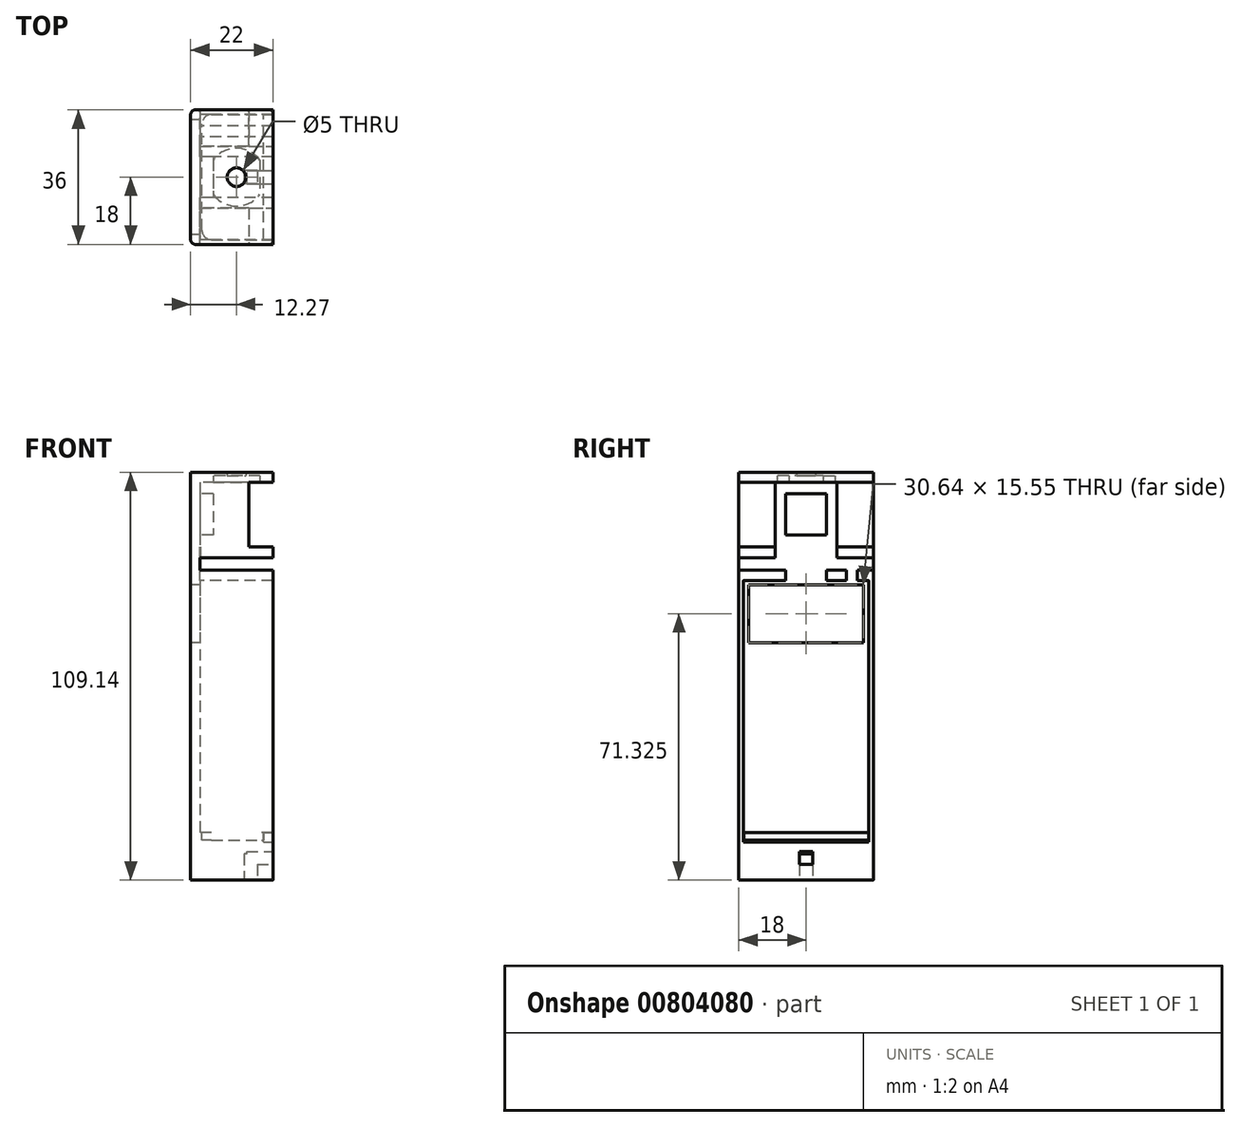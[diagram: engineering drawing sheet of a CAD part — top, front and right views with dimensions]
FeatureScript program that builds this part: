
annotation { "Feature Type Name" : "Feature", "Feature Type Description" : "" }
export const myFeature = defineFeature(function(context is Context, id is Id, definition is map)
    precondition{}
    {
        {
            var Q0;
            Q0=qCreatedBy(makeId("Right.planeOp"),FACE);
            var sketch = newSketch(context, id + "F0", { "sketchPlane" : qUnion([Q0])});
            skLineSegment(sketch, "E0", {"start": v(0, 0) * mm, "end": v(0, 70.44) * mm});
            skLineSegment(sketch, "E1", {"start": v(0, 70.44) * mm, "end": v(0, -68.16) * mm});
            skSolve(sketch);
        }
        {
            var Q0;
            Q0=qCreatedBy(makeId("Right.planeOp"),FACE);
            var sketch = newSketch(context, id + "F1", { "sketchPlane" : qUnion([Q0])});
            skLineSegment(sketch, "E2", {"start": v(0, 0) * mm, "end": v(-18, 0) * mm});
            skLineSegment(sketch, "E3", {"start": v(-18, 0) * mm, "end": v(-18, 100) * mm});
            skLineSegment(sketch, "E4", {"start": v(-18, 100) * mm, "end": v(0, 100) * mm});
            skLineSegment(sketch, "E5.MirrorCS", {"start": v(18, 100) * mm, "end": v(0, 100) * mm});
            skLineSegment(sketch, "E6.MirrorCS", {"start": v(0, 0) * mm, "end": v(18, 0) * mm});
            skLineSegment(sketch, "E7.MirrorCS", {"start": v(18, 0) * mm, "end": v(18, 100) * mm});
            skSolve(sketch);
        }
        {
            var Q0;
            Q0=makeQuery(id+"F1.imprint","IMPRINT",FACE,{"disambiguationData":[TD([[makeQuery(id+"F1.imprint","IMPRINT",EDGE,{"derivedFrom":sQuery(id+"F1.wireOp",EDGE,"E2")}),-1.0]])]});
            extrude(context, id + "F2", {"entities" : qUnion([Q0]), "oppositeDirection" : true, "depth" : 22 * mm, "offsetDistance" : 25.4 * mm});
        }
        {
            var Q0;
            Q0=makeQuery(id+"F2.opExtrude","CAP_FACE",FACE,{"disambiguationData":[OSD([sQuery(id+"F1.wireOp",EDGE,"E2"),sQuery(id+"F1.wireOp",EDGE,"E3"),sQuery(id+"F1.wireOp",EDGE,"E4"),sQuery(id+"F1.wireOp",EDGE,"E5.MirrorCS"),sQuery(id+"F1.wireOp",EDGE,"E6.MirrorCS"),sQuery(id+"F1.wireOp",EDGE,"E7.MirrorCS")])],"isStart":true});
            var Q1;
            Q1=makeQuery(id+"F2.opExtrude","SWEPT_FACE",FACE,{"disambiguationData":[OSD([sQuery(id+"F1.wireOp",EDGE,"E7.MirrorCS")])]});
            var Q2;
            Q2=makeQuery(id+"F2.opExtrude","SWEPT_FACE",FACE,{"disambiguationData":[OSD([sQuery(id+"F1.wireOp",EDGE,"E3")])]});
            shell(context, id + "F3", {"entities" : qUnion([Q0, Q1, Q2]), "thickness" : 2.54 * mm});
        }
        {
            var Q0;
            Q0=makeQuery(id+"F3.opShell","OFFSET_FACE",FACE,{"disambiguationData":[OSD([sQuery(id+"F1.wireOp",EDGE,"E2"),sQuery(id+"F1.wireOp",EDGE,"E6.MirrorCS")])]});
            var sketch = newSketch(context, id + "F4", { "sketchPlane" : qUnion([Q0])});
            skLineSegment(sketch, "E8.bottom", {"start": v(-18.98, -16.75) * mm, "end": v(-0.48, -16.75) * mm});
            skLineSegment(sketch, "E8.top", {"start": v(-18.98, 16.75) * mm, "end": v(-0.48, 16.75) * mm});
            skLineSegment(sketch, "E8.left", {"start": v(-18.98, -16.75) * mm, "end": v(-18.98, 16.75) * mm});
            skLineSegment(sketch, "E8.right", {"start": v(-0.48, -16.75) * mm, "end": v(-0.48, 16.75) * mm});
            skLineSegment(sketch, "E9", {"start": v(0, 0) * mm, "end": v(-19.46, 0) * mm});
            skLineSegment(sketch, "E10", {"start": v(-9.73, -18) * mm, "end": v(-9.73, 18) * mm});
            skSolve(sketch);
        }
        {
            var Q0;
            Q0 = qSketchRegion(id + "F4", true);
            extrude(context, id + "F5", {"entities" : qUnion([Q0]), "operationType" : NewBodyOperationType.REMOVE, "oppositeDirection" : true, "depth" : 2 * mm, "offsetDistance" : 25.4 * mm});
        }
        {
            var Q0;
            Q0=makeQuery(id+"F5.boolean.opBoolean","COPY",EDGE,{"derivedFrom":makeQuery(id+"F5.opExtrude","SWEPT_EDGE",EDGE,{"disambiguationData":[OSD([sQuery(id+"F4.wireOp",EDGE,"E8.bottom"),sQuery(id+"F4.wireOp",EDGE,"E8.left")])]})});
            var Q1;
            Q1=makeQuery(id+"F5.boolean.opBoolean","COPY",EDGE,{"derivedFrom":makeQuery(id+"F5.opExtrude","SWEPT_EDGE",EDGE,{"disambiguationData":[OSD([sQuery(id+"F4.wireOp",EDGE,"E8.top"),sQuery(id+"F4.wireOp",EDGE,"E8.left")])]})});
            var Q2;
            Q2=makeQuery(id+"F5.boolean.opBoolean","COPY",EDGE,{"derivedFrom":makeQuery(id+"F5.opExtrude","SWEPT_EDGE",EDGE,{"disambiguationData":[OSD([sQuery(id+"F4.wireOp",EDGE,"E8.top"),sQuery(id+"F4.wireOp",EDGE,"E8.right")])]})});
            var Q3;
            Q3=makeQuery(id+"F5.boolean.opBoolean","COPY",EDGE,{"derivedFrom":makeQuery(id+"F5.opExtrude","SWEPT_EDGE",EDGE,{"disambiguationData":[OSD([sQuery(id+"F4.wireOp",EDGE,"E8.bottom"),sQuery(id+"F4.wireOp",EDGE,"E8.right")])]})});
            fillet(context, id + "F6", {"entities" : qUnion([Q0, Q1, Q2, Q3]), "radius" : 2.54 * mm, "tangentPropagation" : true, "allowEdgeOverflow" : false});
        }
        {
            var Q0;
            {var subQ0=sQuery(id+"F1.wireOp",EDGE,"E7.MirrorCS");var subQ1=sQuery(id+"F1.wireOp",EDGE,"E6.MirrorCS");var subQ2=sQuery(id+"F1.wireOp",EDGE,"E5.MirrorCS");var subQ3=sQuery(id+"F1.wireOp",EDGE,"E4");var subQ4=sQuery(id+"F1.wireOp",EDGE,"E3");var subQ5=sQuery(id+"F1.wireOp",EDGE,"E2");Q0=makeQuery(id+"F3.opShell","OFFSET_FACE",FACE,{"disambiguationData":[OSD([subQ5,subQ4,subQ3,subQ2,subQ1,subQ0]),TDD([makeQuery(id+"F2.opExtrude","CAP_FACE",FACE,{"disambiguationData":[OSD([subQ5,subQ4,subQ3,subQ2,subQ1,subQ0])],"isStart":false})])]});}
            var sketch = newSketch(context, id + "F7", { "sketchPlane" : qUnion([Q0])});
            skLineSegment(sketch, "E11.bottom", {"start": v(-18, 70.04) * mm, "end": v(-5.5, 70.04) * mm});
            skLineSegment(sketch, "E11.top", {"start": v(-18, 72.77) * mm, "end": v(-5.5, 72.77) * mm});
            skLineSegment(sketch, "E11.left", {"start": v(-18, 70.04) * mm, "end": v(-18, 72.77) * mm});
            skLineSegment(sketch, "E11.right", {"start": v(-5.5, 70.04) * mm, "end": v(-5.5, 72.77) * mm});
            skLineSegment(sketch, "E12.bottom", {"start": v(5.5, 72.77) * mm, "end": v(10.75, 72.77) * mm});
            skLineSegment(sketch, "E12.top", {"start": v(5.5, 70.04) * mm, "end": v(10.75, 70.04) * mm});
            skLineSegment(sketch, "E12.left", {"start": v(5.5, 72.77) * mm, "end": v(5.5, 70.04) * mm});
            skLineSegment(sketch, "E12.right", {"start": v(10.75, 72.77) * mm, "end": v(10.75, 70.04) * mm});
            skLineSegment(sketch, "E13", {"start": v(-16.75, 70.04) * mm, "end": v(-16.75, 72.77) * mm});
            skPoint(sketch, "E14.end.orphan", {"position": v(-14.33, 70.04) * mm});
            skLineSegment(sketch, "E15.bottom", {"start": v(18, 70.04) * mm, "end": v(13.7, 70.04) * mm});
            skLineSegment(sketch, "E15.top", {"start": v(18, 72.77) * mm, "end": v(13.7, 72.77) * mm});
            skLineSegment(sketch, "E15.left", {"start": v(18, 70.04) * mm, "end": v(18, 72.77) * mm});
            skLineSegment(sketch, "E15.right", {"start": v(13.7, 70.04) * mm, "end": v(13.7, 72.77) * mm});
            skLineSegment(sketch, "E16.bottom", {"start": v(-18, 76.1) * mm, "end": v(-5.5, 76.1) * mm});
            skLineSegment(sketch, "E16.top", {"start": v(-18, 79.1) * mm, "end": v(-5.5, 79.1) * mm});
            skLineSegment(sketch, "E16.left", {"start": v(-18, 76.1) * mm, "end": v(-18, 79.1) * mm});
            skLineSegment(sketch, "E16.right", {"start": v(-5.5, 76.1) * mm, "end": v(-5.5, 79.1) * mm});
            skLineSegment(sketch, "E17.bottom", {"start": v(5.5, 76.1) * mm, "end": v(18, 76.1) * mm});
            skLineSegment(sketch, "E17.top", {"start": v(5.5, 79.1) * mm, "end": v(18, 79.1) * mm});
            skLineSegment(sketch, "E17.left", {"start": v(5.5, 76.1) * mm, "end": v(5.5, 79.1) * mm});
            skLineSegment(sketch, "E17.right", {"start": v(18, 76.1) * mm, "end": v(18, 79.1) * mm});
            skSolve(sketch);
        }
        {
            var Q0;
            Q0=makeQuery(id+"F3.opShell","OFFSET_FACE",FACE,{"disambiguationData":[OSD([sQuery(id+"F1.wireOp",EDGE,"E4"),sQuery(id+"F1.wireOp",EDGE,"E5.MirrorCS")])]});
            var sketch = newSketch(context, id + "F8", { "sketchPlane" : qUnion([Q0])});
            skArc(sketch, "E18", {"start": v(-3.48, 4.58) * mm, "mid": v(-9.73, 7.75) * mm, "end": v(-15.98, 4.58) * mm});
            skPoint(sketch, "E18.centerSnap0", {"position": v(-19.46, 0) * mm});
            skPoint(sketch, "E18.centerSnap1", {"position": v(-9.73, -18) * mm});
            skLineSegment(sketch, "E19.bottom", {"start": v(-3.48, -4.58) * mm, "end": v(-15.98, -4.58) * mm});
            skLineSegment(sketch, "E19.top", {"start": v(-3.48, 4.58) * mm, "end": v(-15.98, 4.58) * mm});
            skLineSegment(sketch, "E19.left", {"start": v(-3.48, -4.58) * mm, "end": v(-3.48, 4.58) * mm});
            skLineSegment(sketch, "E19.right", {"start": v(-15.98, -4.58) * mm, "end": v(-15.98, 4.58) * mm});
            skArc(sketch, "E20.trimOffspring", {"start": v(-15.98, -4.58) * mm, "mid": v(-9.73, -7.75) * mm, "end": v(-3.48, -4.58) * mm});
            skSolve(sketch);
        }
        {
            var Q0;
            Q0 = qSketchRegion(id + "F8", true);
            extrude(context, id + "F9", {"entities" : qUnion([Q0]), "operationType" : NewBodyOperationType.REMOVE, "oppositeDirection" : true, "depth" : 0.64 * mm, "offsetDistance" : 25.4 * mm});
        }
        {
            var Q0;
            Q0 = qSketchRegion(id + "F7", true);
            extrude(context, id + "F10", {"entities" : qUnion([Q0]), "operationType" : NewBodyOperationType.ADD, "depth" : 19.46 * mm, "offsetDistance" : 25.4 * mm});
        }
        {
            var Q0;
            Q0=makeQuery(id+"F9.boolean.opBoolean","COPY",FACE,{"derivedFrom":makeQuery(id+"F9.opExtrude","CAP_FACE",FACE,{"disambiguationData":[OSD([sQuery(id+"F8.wireOp",EDGE,"E18"),sQuery(id+"F8.wireOp",EDGE,"E19.left"),sQuery(id+"F8.wireOp",EDGE,"E19.right"),sQuery(id+"F8.wireOp",EDGE,"E20.trimOffspring")])],"isStart":false})});
            var sketch = newSketch(context, id + "F11", { "sketchPlane" : qUnion([Q0])});
            skCircle(sketch, "E21", {"center": v(-9.73, 0) * mm, "radius": 2.5 * mm});
            skSolve(sketch);
        }
        {
            var Q0;
            Q0=makeQuery(id+"F11.imprint","IMPRINT",FACE,{"disambiguationData":[TD([[makeQuery(id+"F11.imprint","IMPRINT",EDGE,{"derivedFrom":sQuery(id+"F11.wireOp",EDGE,"E21")}),1.0]])]});
            extrude(context, id + "F12", {"entities" : qUnion([Q0]), "operationType" : NewBodyOperationType.REMOVE, "oppositeDirection" : true, "depth" : 2.26 * mm, "offsetDistance" : 25.4 * mm});
        }
        {
            var Q0;
            Q0=makeQuery(id+"F3.opShell","OFFSET_FACE",FACE,{"disambiguationData":[OSD([sQuery(id+"F1.wireOp",EDGE,"E4"),sQuery(id+"F1.wireOp",EDGE,"E5.MirrorCS")])]});
            extrude(context, id + "F13", {"entities" : qUnion([Q0]), "operationType" : NewBodyOperationType.ADD, "depth" : 1.14 * mm, "offsetDistance" : 25.4 * mm});
        }
        {
            var Q0;
            Q0=makeQuery(id+"F2.opExtrude","SWEPT_FACE",FACE,{"disambiguationData":[OSD([sQuery(id+"F1.wireOp",EDGE,"E4"),sQuery(id+"F1.wireOp",EDGE,"E5.MirrorCS")])]});
            extrude(context, id + "F14", {"entities" : qUnion([Q0]), "operationType" : NewBodyOperationType.REMOVE, "oppositeDirection" : true, "depth" : 1.02 * mm, "offsetDistance" : 25.4 * mm});
        }
        {
            var Q0;
            {var subQ0=sQuery(id+"F1.wireOp",EDGE,"E7.MirrorCS");var subQ1=sQuery(id+"F1.wireOp",EDGE,"E6.MirrorCS");var subQ2=sQuery(id+"F1.wireOp",EDGE,"E5.MirrorCS");var subQ3=sQuery(id+"F1.wireOp",EDGE,"E4");var subQ4=sQuery(id+"F1.wireOp",EDGE,"E3");var subQ5=sQuery(id+"F1.wireOp",EDGE,"E2");Q0=makeQuery(id+"F3.opShell","OFFSET_FACE",FACE,{"disambiguationData":[OSD([subQ5,subQ4,subQ3,subQ2,subQ1,subQ0]),TDD([makeQuery(id+"F2.opExtrude","CAP_FACE",FACE,{"disambiguationData":[OSD([subQ5,subQ4,subQ3,subQ2,subQ1,subQ0])],"isStart":false})])]});}
            var sketch = newSketch(context, id + "F15", { "sketchPlane" : qUnion([Q0])});
            skLineSegment(sketch, "E22", {"start": v(0, 87.22) * mm, "end": v(-8.25, 87.22) * mm});
            skLineSegment(sketch, "E23", {"start": v(-8.25, 87.22) * mm, "end": v(8.25, 87.22) * mm});
            skLineSegment(sketch, "E24.bottom", {"start": v(18, 96.32) * mm, "end": v(8.25, 96.32) * mm});
            skLineSegment(sketch, "E24.top", {"start": v(18, 79.1) * mm, "end": v(8.25, 79.1) * mm});
            skLineSegment(sketch, "E24.left", {"start": v(18, 96.32) * mm, "end": v(18, 79.1) * mm});
            skLineSegment(sketch, "E24.right", {"start": v(8.25, 96.32) * mm, "end": v(8.25, 79.1) * mm});
            skLineSegment(sketch, "E25.bottom", {"start": v(-8.25, 79.1) * mm, "end": v(-18, 79.1) * mm});
            skLineSegment(sketch, "E25.top", {"start": v(-8.25, 96.32) * mm, "end": v(-18, 96.32) * mm});
            skLineSegment(sketch, "E25.left", {"start": v(-8.25, 79.1) * mm, "end": v(-8.25, 96.32) * mm});
            skLineSegment(sketch, "E25.right", {"start": v(-18, 79.1) * mm, "end": v(-18, 96.32) * mm});
            skSolve(sketch);
        }
        {
            var Q0;
            Q0 = qSketchRegion(id + "F15", true);
            extrude(context, id + "F16", {"entities" : qUnion([Q0]), "operationType" : NewBodyOperationType.ADD, "depth" : 13 * mm, "offsetDistance" : 25.4 * mm});
        }
        {
            var Q0;
            {var subQ0=sQuery(id+"F1.wireOp",EDGE,"E7.MirrorCS");var subQ1=sQuery(id+"F1.wireOp",EDGE,"E6.MirrorCS");var subQ2=sQuery(id+"F1.wireOp",EDGE,"E5.MirrorCS");var subQ3=sQuery(id+"F1.wireOp",EDGE,"E4");var subQ4=sQuery(id+"F1.wireOp",EDGE,"E3");var subQ5=sQuery(id+"F1.wireOp",EDGE,"E2");Q0=makeQuery(id+"F3.opShell","OFFSET_FACE",FACE,{"disambiguationData":[OSD([subQ5,subQ4,subQ3,subQ2,subQ1,subQ0]),TDD([makeQuery(id+"F2.opExtrude","CAP_FACE",FACE,{"disambiguationData":[OSD([subQ5,subQ4,subQ3,subQ2,subQ1,subQ0])],"isStart":false})])]});}
            var sketch = newSketch(context, id + "F17", { "sketchPlane" : qUnion([Q0])});
            skLineSegment(sketch, "E26.bottom", {"start": v(-18, 2.54) * mm, "end": v(-16.75, 2.54) * mm});
            skLineSegment(sketch, "E26.top", {"start": v(-18, 70.04) * mm, "end": v(-16.75, 70.04) * mm});
            skLineSegment(sketch, "E26.left", {"start": v(-18, 2.54) * mm, "end": v(-18, 70.04) * mm});
            skLineSegment(sketch, "E26.right", {"start": v(-16.75, 2.54) * mm, "end": v(-16.75, 70.04) * mm});
            skLineSegment(sketch, "E27.bottom", {"start": v(18, 70.04) * mm, "end": v(16.75, 70.04) * mm});
            skLineSegment(sketch, "E27.top", {"start": v(18, 2.54) * mm, "end": v(16.75, 2.54) * mm});
            skLineSegment(sketch, "E27.left", {"start": v(18, 70.04) * mm, "end": v(18, 2.54) * mm});
            skLineSegment(sketch, "E27.right", {"start": v(16.75, 70.04) * mm, "end": v(16.75, 2.54) * mm});
            skSolve(sketch);
        }
        {
            var Q0;
            Q0 = qSketchRegion(id + "F17", true);
            extrude(context, id + "F18", {"entities" : qUnion([Q0]), "operationType" : NewBodyOperationType.ADD, "depth" : 19.46 * mm, "offsetDistance" : 25.4 * mm});
        }
        {
            var Q0;
            Q0=makeQuery(id+"F2.opExtrude","CAP_EDGE",EDGE,{"disambiguationData":[OSD([sQuery(id+"F1.wireOp",EDGE,"E7.MirrorCS")])],"isStart":false});
            var Q1;
            Q1=makeQuery(id+"F2.opExtrude","CAP_EDGE",EDGE,{"disambiguationData":[OSD([sQuery(id+"F1.wireOp",EDGE,"E3")])],"isStart":false});
            var Q2;
            Q2=makeQuery(id+"F18.boolean.opBoolean","MERGE",EDGE,{"derivedFrom":[makeQuery(id+"F2.opExtrude","CAP_EDGE",EDGE,{"disambiguationData":[OSD([sQuery(id+"F1.wireOp",EDGE,"E3")])],"isStart":true}),makeQuery(id+"F10.opExtrude","CAP_EDGE",EDGE,{"disambiguationData":[OSD([sQuery(id+"F7.wireOp",EDGE,"E11.left")])],"isStart":false}),makeQuery(id+"F18.opExtrude","CAP_EDGE",EDGE,{"disambiguationData":[OSD([sQuery(id+"F17.wireOp",EDGE,"E26.left")])],"isStart":false})]});
            var Q3;
            Q3=makeQuery(id+"F18.boolean.opBoolean","MERGE",EDGE,{"derivedFrom":[makeQuery(id+"F2.opExtrude","CAP_EDGE",EDGE,{"disambiguationData":[OSD([sQuery(id+"F1.wireOp",EDGE,"E7.MirrorCS")])],"isStart":true}),makeQuery(id+"F10.opExtrude","CAP_EDGE",EDGE,{"disambiguationData":[OSD([sQuery(id+"F7.wireOp",EDGE,"E15.left")])],"isStart":false}),makeQuery(id+"F18.opExtrude","CAP_EDGE",EDGE,{"disambiguationData":[OSD([sQuery(id+"F17.wireOp",EDGE,"E27.left")])],"isStart":false})]});
            var Q4;
            Q4=makeQuery(id+"F14.boolean.opBoolean","COPY",EDGE,{"derivedFrom":makeQuery(id+"F14.opExtrude","CAP_EDGE",EDGE,{"disambiguationData":[OSD([sQuery(id+"F1.wireOp",EDGE,"E5.MirrorCS"),sQuery(id+"F1.wireOp",EDGE,"E7.MirrorCS")])],"isStart":false})});
            var Q5;
            Q5=makeQuery(id+"F14.boolean.opBoolean","COPY",EDGE,{"derivedFrom":makeQuery(id+"F14.opExtrude","CAP_EDGE",EDGE,{"disambiguationData":[OSD([sQuery(id+"F1.wireOp",EDGE,"E3"),sQuery(id+"F1.wireOp",EDGE,"E4")])],"isStart":false})});
            var Q6;
            {var subQ0=sQuery(id+"F1.wireOp",EDGE,"E5.MirrorCS");var subQ1=sQuery(id+"F1.wireOp",EDGE,"E4");Q6=makeQuery(id+"F14.boolean.opBoolean","COPY",EDGE,{"derivedFrom":makeQuery(id+"F14.opExtrude","CAP_EDGE",EDGE,{"disambiguationData":[OSD([subQ1,subQ0]),TDD([makeQuery(id+"F2.opExtrude","CAP_EDGE",EDGE,{"disambiguationData":[OSD([subQ1,subQ0])],"isStart":false})])],"isStart":false})});}
            fillet(context, id + "F19", {"entities" : qUnion([Q0, Q1, Q2, Q3, Q4, Q5, Q6]), "radius" : 1.27 * mm, "tangentPropagation" : true, "allowEdgeOverflow" : false});
        }
        {
            var Q0;
            Q0=makeQuery(id+"F2.opExtrude","SWEPT_FACE",FACE,{"disambiguationData":[OSD([sQuery(id+"F1.wireOp",EDGE,"E2"),sQuery(id+"F1.wireOp",EDGE,"E6.MirrorCS")])]});
            var sketch = newSketch(context, id + "F20", { "sketchPlane" : qUnion([Q0])});
            skSolve(sketch);
        }
        {
            var Q0;
            Q0 = qSketchRegion(id + "F20", true);
            var Q1;
            {var subQ1=sQuery(id+"F1.wireOp",EDGE,"E2");var subQ3=sQuery(id+"F1.wireOp",EDGE,"E3");Q1=makeQuery(id+"F20.imprint","IMPRINT",FACE,{"disambiguationData":[TD([[makeQuery(id+"F20.imprint","IMPRINT",EDGE,{"derivedFrom":makeQuery(id+"F2.opExtrude","SWEPT_EDGE",EDGE,{"disambiguationData":[OSD([subQ1,subQ3])]})}),-1.0]])]});}
            extrude(context, id + "F21", {"entities" : qUnion([Q0, Q1]), "operationType" : NewBodyOperationType.ADD, "depth" : 10.16 * mm, "offsetDistance" : 25.4 * mm});
        }
        {
            var Q0;
            {var subQ0=sQuery(id+"F1.wireOp",EDGE,"E6.MirrorCS");var subQ1=sQuery(id+"F1.wireOp",EDGE,"E2");var subQ2=sQuery(id+"F1.wireOp",EDGE,"E7.MirrorCS");var subQ3=sQuery(id+"F1.wireOp",EDGE,"E5.MirrorCS");var subQ4=sQuery(id+"F1.wireOp",EDGE,"E4");var subQ5=sQuery(id+"F1.wireOp",EDGE,"E3");Q0=makeQuery(id+"F21.boolean.opBoolean","MERGE",FACE,{"derivedFrom":[makeQuery(id+"F19.opFillet","SPLIT",FACE,{"disambiguationData":[OD(2.0)],"derivedFrom":makeQuery(id+"F18.boolean.opBoolean","MERGE",FACE,{"derivedFrom":[makeQuery(id+"F3.opShell","OFFSET_FACE",FACE,{"disambiguationData":[OSD([subQ1,subQ5,subQ4,subQ3,subQ0,subQ2]),TDD([makeQuery(id+"F2.opExtrude","CAP_FACE",FACE,{"disambiguationData":[OSD([subQ1,subQ5,subQ4,subQ3,subQ0,subQ2])],"isStart":true})])]}),makeQuery(id+"F10.opExtrude","CAP_FACE",FACE,{"disambiguationData":[OSD([sQuery(id+"F7.wireOp",EDGE,"E11.bottom"),sQuery(id+"F7.wireOp",EDGE,"E11.top"),sQuery(id+"F7.wireOp",EDGE,"E11.left"),sQuery(id+"F7.wireOp",EDGE,"E11.right")])],"isStart":false}),makeQuery(id+"F10.opExtrude","CAP_FACE",FACE,{"disambiguationData":[OSD([sQuery(id+"F7.wireOp",EDGE,"E15.bottom"),sQuery(id+"F7.wireOp",EDGE,"E15.top"),sQuery(id+"F7.wireOp",EDGE,"E15.left"),sQuery(id+"F7.wireOp",EDGE,"E15.right")])],"isStart":false}),makeQuery(id+"F18.opExtrude","CAP_FACE",FACE,{"disambiguationData":[OSD([sQuery(id+"F17.wireOp",EDGE,"E26.bottom"),sQuery(id+"F17.wireOp",EDGE,"E26.top"),sQuery(id+"F17.wireOp",EDGE,"E26.left"),sQuery(id+"F17.wireOp",EDGE,"E26.right")])],"isStart":false}),makeQuery(id+"F18.opExtrude","CAP_FACE",FACE,{"disambiguationData":[OSD([sQuery(id+"F17.wireOp",EDGE,"E27.bottom"),sQuery(id+"F17.wireOp",EDGE,"E27.top"),sQuery(id+"F17.wireOp",EDGE,"E27.left"),sQuery(id+"F17.wireOp",EDGE,"E27.right")])],"isStart":false})]})}),makeQuery(id+"F21.opExtrude","SWEPT_FACE",FACE,{"disambiguationData":[OSD([subQ1,subQ0]),TDD([makeQuery(id+"F20.imprint","IMPRINT",EDGE,{"derivedFrom":makeQuery(id+"F2.opExtrude","CAP_EDGE",EDGE,{"disambiguationData":[OSD([subQ1,subQ0])],"isStart":true})})])]})]});}
            var sketch = newSketch(context, id + "F22", { "sketchPlane" : qUnion([Q0])});
            skLineSegment(sketch, "E28.bottom", {"start": v(1.75, -5.97) * mm, "end": v(-1.75, -5.97) * mm});
            skLineSegment(sketch, "E28.top", {"start": v(1.75, -2.47) * mm, "end": v(-1.75, -2.47) * mm});
            skLineSegment(sketch, "E28.left", {"start": v(1.75, -5.97) * mm, "end": v(1.75, -2.47) * mm});
            skLineSegment(sketch, "E28.right", {"start": v(-1.75, -5.97) * mm, "end": v(-1.75, -2.47) * mm});
            skPoint(sketch, "E28.middle", {"position": v(0, -4.22) * mm});
            skSolve(sketch);
        }
        {
            var Q0;
            Q0 = qSketchRegion(id + "F22", true);
            extrude(context, id + "F23", {"entities" : qUnion([Q0]), "operationType" : NewBodyOperationType.REMOVE, "oppositeDirection" : true, "depth" : 7 * mm, "offsetDistance" : 25.4 * mm});
        }
        {
            var Q0;
            Q0=makeQuery(id+"F21.opExtrude","CAP_FACE",FACE,{"disambiguationData":[OSD([sQuery(id+"F1.wireOp",EDGE,"E2"),sQuery(id+"F1.wireOp",EDGE,"E3"),sQuery(id+"F1.wireOp",EDGE,"E6.MirrorCS"),sQuery(id+"F1.wireOp",EDGE,"E7.MirrorCS"),sQuery(id+"F7.wireOp",EDGE,"E11.left"),sQuery(id+"F7.wireOp",EDGE,"E15.left"),sQuery(id+"F17.wireOp",EDGE,"E26.left"),sQuery(id+"F17.wireOp",EDGE,"E27.left")])],"isStart":false});
            var sketch = newSketch(context, id + "F24", { "sketchPlane" : qUnion([Q0])});
            skLineSegment(sketch, "E29.bottom", {"start": v(-4.19, -1.75) * mm, "end": v(-7.69, -1.75) * mm});
            skLineSegment(sketch, "E29.top", {"start": v(-4.19, 1.75) * mm, "end": v(-7.69, 1.75) * mm});
            skLineSegment(sketch, "E29.left", {"start": v(-4.19, -1.75) * mm, "end": v(-4.19, 1.75) * mm});
            skLineSegment(sketch, "E29.right", {"start": v(-7.69, -1.75) * mm, "end": v(-7.69, 1.75) * mm});
            skPoint(sketch, "E29.middle", {"position": v(-5.94, 0) * mm});
            skSolve(sketch);
        }
        {
            var Q0;
            Q0 = qSketchRegion(id + "F24", true);
            extrude(context, id + "F25", {"entities" : qUnion([Q0]), "operationType" : NewBodyOperationType.REMOVE, "oppositeDirection" : true, "depth" : 7 * mm, "offsetDistance" : 25.4 * mm});
        }
        {
            var Q0;
            {var subQ0=sQuery(id+"F1.wireOp",EDGE,"E6.MirrorCS");var subQ1=sQuery(id+"F1.wireOp",EDGE,"E2");Q0=makeQuery(id+"F21.boolean.opBoolean","MERGE",FACE,{"derivedFrom":[makeQuery(id+"F2.opExtrude","CAP_FACE",FACE,{"disambiguationData":[OSD([subQ1,sQuery(id+"F1.wireOp",EDGE,"E3"),sQuery(id+"F1.wireOp",EDGE,"E4"),sQuery(id+"F1.wireOp",EDGE,"E5.MirrorCS"),subQ0,sQuery(id+"F1.wireOp",EDGE,"E7.MirrorCS")])],"isStart":false}),makeQuery(id+"F21.opExtrude","SWEPT_FACE",FACE,{"disambiguationData":[OSD([subQ1,subQ0]),TDD([makeQuery(id+"F20.imprint","IMPRINT",EDGE,{"derivedFrom":makeQuery(id+"F2.opExtrude","CAP_EDGE",EDGE,{"disambiguationData":[OSD([subQ1,subQ0])],"isStart":false})})])]})]});}
            var sketch = newSketch(context, id + "F26", { "sketchPlane" : qUnion([Q0])});
            skLineSegment(sketch, "E30.bottom", {"start": v(-15.32, 68.94) * mm, "end": v(15.32, 68.94) * mm});
            skLineSegment(sketch, "E30.top", {"start": v(-15.32, 53.39) * mm, "end": v(15.32, 53.39) * mm});
            skLineSegment(sketch, "E30.left", {"start": v(-15.32, 68.94) * mm, "end": v(-15.32, 53.39) * mm});
            skLineSegment(sketch, "E30.right", {"start": v(15.32, 68.94) * mm, "end": v(15.32, 53.39) * mm});
            skSolve(sketch);
        }
        {
            var Q0;
            Q0 = qSketchRegion(id + "F26", true);
            extrude(context, id + "F27", {"entities" : qUnion([Q0]), "operationType" : NewBodyOperationType.REMOVE, "oppositeDirection" : true, "depth" : 2.54 * mm, "offsetDistance" : 25.4 * mm});
        }
        {
            var Q0;
            {var subQ0=sQuery(id+"F1.wireOp",EDGE,"E6.MirrorCS");var subQ1=sQuery(id+"F1.wireOp",EDGE,"E2");var subQ2=sQuery(id+"F1.wireOp",EDGE,"E7.MirrorCS");var subQ3=sQuery(id+"F1.wireOp",EDGE,"E5.MirrorCS");var subQ4=sQuery(id+"F1.wireOp",EDGE,"E4");var subQ5=sQuery(id+"F1.wireOp",EDGE,"E3");Q0=makeQuery(id+"F21.boolean.opBoolean","MERGE",FACE,{"derivedFrom":[makeQuery(id+"F19.opFillet","SPLIT",FACE,{"disambiguationData":[OD(2.0)],"derivedFrom":makeQuery(id+"F18.boolean.opBoolean","MERGE",FACE,{"derivedFrom":[makeQuery(id+"F3.opShell","OFFSET_FACE",FACE,{"disambiguationData":[OSD([subQ1,subQ5,subQ4,subQ3,subQ0,subQ2]),TDD([makeQuery(id+"F2.opExtrude","CAP_FACE",FACE,{"disambiguationData":[OSD([subQ1,subQ5,subQ4,subQ3,subQ0,subQ2])],"isStart":true})])]}),makeQuery(id+"F10.opExtrude","CAP_FACE",FACE,{"disambiguationData":[OSD([sQuery(id+"F7.wireOp",EDGE,"E11.bottom"),sQuery(id+"F7.wireOp",EDGE,"E11.top"),sQuery(id+"F7.wireOp",EDGE,"E11.left"),sQuery(id+"F7.wireOp",EDGE,"E11.right")])],"isStart":false}),makeQuery(id+"F10.opExtrude","CAP_FACE",FACE,{"disambiguationData":[OSD([sQuery(id+"F7.wireOp",EDGE,"E15.bottom"),sQuery(id+"F7.wireOp",EDGE,"E15.top"),sQuery(id+"F7.wireOp",EDGE,"E15.left"),sQuery(id+"F7.wireOp",EDGE,"E15.right")])],"isStart":false}),makeQuery(id+"F18.opExtrude","CAP_FACE",FACE,{"disambiguationData":[OSD([sQuery(id+"F17.wireOp",EDGE,"E26.bottom"),sQuery(id+"F17.wireOp",EDGE,"E26.top"),sQuery(id+"F17.wireOp",EDGE,"E26.left"),sQuery(id+"F17.wireOp",EDGE,"E26.right")])],"isStart":false}),makeQuery(id+"F18.opExtrude","CAP_FACE",FACE,{"disambiguationData":[OSD([sQuery(id+"F17.wireOp",EDGE,"E27.bottom"),sQuery(id+"F17.wireOp",EDGE,"E27.top"),sQuery(id+"F17.wireOp",EDGE,"E27.left"),sQuery(id+"F17.wireOp",EDGE,"E27.right")])],"isStart":false})]})}),makeQuery(id+"F21.opExtrude","SWEPT_FACE",FACE,{"disambiguationData":[OSD([subQ1,subQ0]),TDD([makeQuery(id+"F20.imprint","IMPRINT",EDGE,{"derivedFrom":makeQuery(id+"F2.opExtrude","CAP_EDGE",EDGE,{"disambiguationData":[OSD([subQ1,subQ0])],"isStart":true})})])]})]});}
            var sketch = newSketch(context, id + "F28", { "sketchPlane" : qUnion([Q0])});
            skLineSegment(sketch, "E31.bottom", {"start": v(-16.73, 2.54) * mm, "end": v(16.73, 2.54) * mm});
            skLineSegment(sketch, "E31.top", {"start": v(-16.73, 0) * mm, "end": v(16.73, 0) * mm});
            skLineSegment(sketch, "E31.left", {"start": v(-16.73, 2.54) * mm, "end": v(-16.73, 0) * mm});
            skLineSegment(sketch, "E31.right", {"start": v(16.73, 2.54) * mm, "end": v(16.73, 0) * mm});
            skLineSegment(sketch, "E32.top", {"start": v(-16.73, 0.3) * mm, "end": v(16.73, 0.3) * mm});
            skLineSegment(sketch, "E32.left", {"start": v(-16.73, 2.54) * mm, "end": v(-16.73, 0.3) * mm});
            skLineSegment(sketch, "E32.right", {"start": v(16.73, 2.54) * mm, "end": v(16.73, 0.3) * mm});
            skSolve(sketch);
        }
        {
            var Q0;
            Q0 = qSketchRegion(id + "F28", true);
            extrude(context, id + "F29", {"entities" : qUnion([Q0]), "operationType" : NewBodyOperationType.REMOVE, "oppositeDirection" : true, "depth" : 2.54 * mm, "offsetDistance" : 25.4 * mm});
        }
        {
            var Q0;
            Q0=makeQuery(id+"F10.opExtrude","CAP_FACE",FACE,{"disambiguationData":[OSD([sQuery(id+"F7.wireOp",EDGE,"E16.bottom"),sQuery(id+"F7.wireOp",EDGE,"E16.top"),sQuery(id+"F7.wireOp",EDGE,"E16.left"),sQuery(id+"F7.wireOp",EDGE,"E16.right")])],"isStart":false});
            var sketch = newSketch(context, id + "F30", { "sketchPlane" : qUnion([Q0])});
            skLineSegment(sketch, "E33.bottom", {"start": v(-8.25, 79.1) * mm, "end": v(-5.5, 79.1) * mm});
            skLineSegment(sketch, "E33.top", {"start": v(-8.25, 76.1) * mm, "end": v(-5.5, 76.1) * mm});
            skLineSegment(sketch, "E33.left", {"start": v(-8.25, 79.1) * mm, "end": v(-8.25, 76.1) * mm});
            skLineSegment(sketch, "E33.right", {"start": v(-5.5, 79.1) * mm, "end": v(-5.5, 76.1) * mm});
            skLineSegment(sketch, "E34.bottom", {"start": v(8.25, 79.1) * mm, "end": v(5.5, 79.1) * mm});
            skLineSegment(sketch, "E34.top", {"start": v(8.25, 76.1) * mm, "end": v(5.5, 76.1) * mm});
            skLineSegment(sketch, "E34.left", {"start": v(8.25, 79.1) * mm, "end": v(8.25, 76.1) * mm});
            skLineSegment(sketch, "E34.right", {"start": v(5.5, 79.1) * mm, "end": v(5.5, 76.1) * mm});
            skSolve(sketch);
        }
        {
            var Q0;
            Q0 = qSketchRegion(id + "F30", true);
            extrude(context, id + "F31", {"entities" : qUnion([Q0]), "operationType" : NewBodyOperationType.REMOVE, "oppositeDirection" : true, "depth" : 19.46 * mm, "offsetDistance" : 25.4 * mm});
        }
        {
            var Q0;
            {var subQ0=sQuery(id+"F1.wireOp",EDGE,"E7.MirrorCS");var subQ1=sQuery(id+"F1.wireOp",EDGE,"E6.MirrorCS");var subQ2=sQuery(id+"F1.wireOp",EDGE,"E5.MirrorCS");var subQ3=sQuery(id+"F1.wireOp",EDGE,"E4");var subQ4=sQuery(id+"F1.wireOp",EDGE,"E3");var subQ5=sQuery(id+"F1.wireOp",EDGE,"E2");Q0=makeQuery(id+"F3.opShell","OFFSET_FACE",FACE,{"disambiguationData":[OSD([subQ5,subQ4,subQ3,subQ2,subQ1,subQ0]),TDD([makeQuery(id+"F2.opExtrude","CAP_FACE",FACE,{"disambiguationData":[OSD([subQ5,subQ4,subQ3,subQ2,subQ1,subQ0])],"isStart":false})])]});}
            var sketch = newSketch(context, id + "F32", { "sketchPlane" : qUnion([Q0])});
            skLineSegment(sketch, "E35.bottom", {"start": v(5.5, 93.2) * mm, "end": v(-5.5, 93.2) * mm});
            skLineSegment(sketch, "E35.top", {"start": v(5.5, 82.2) * mm, "end": v(-5.5, 82.2) * mm});
            skLineSegment(sketch, "E35.left", {"start": v(5.5, 93.2) * mm, "end": v(5.5, 82.2) * mm});
            skLineSegment(sketch, "E35.right", {"start": v(-5.5, 93.2) * mm, "end": v(-5.5, 82.2) * mm});
            skPoint(sketch, "E35.middle", {"position": v(0, 87.7) * mm});
            skPoint(sketch, "E35.middle.positionSnap0", {"position": v(8.25, 87.7) * mm});
            skPoint(sketch, "E35.middle.positionSnap1", {"position": v(0, 96.32) * mm});
            skPoint(sketch, "E35.centerSnap0", {"position": v(8.25, 87.7) * mm});
            skPoint(sketch, "E35.centerSnap1", {"position": v(0, 96.32) * mm});
            skSolve(sketch);
        }
        {
            var Q0;
            Q0 = qSketchRegion(id + "F32", true);
            extrude(context, id + "F33", {"entities" : qUnion([Q0]), "operationType" : NewBodyOperationType.ADD, "depth" : 3.45 * mm, "offsetDistance" : 25.4 * mm});
        }
    });
